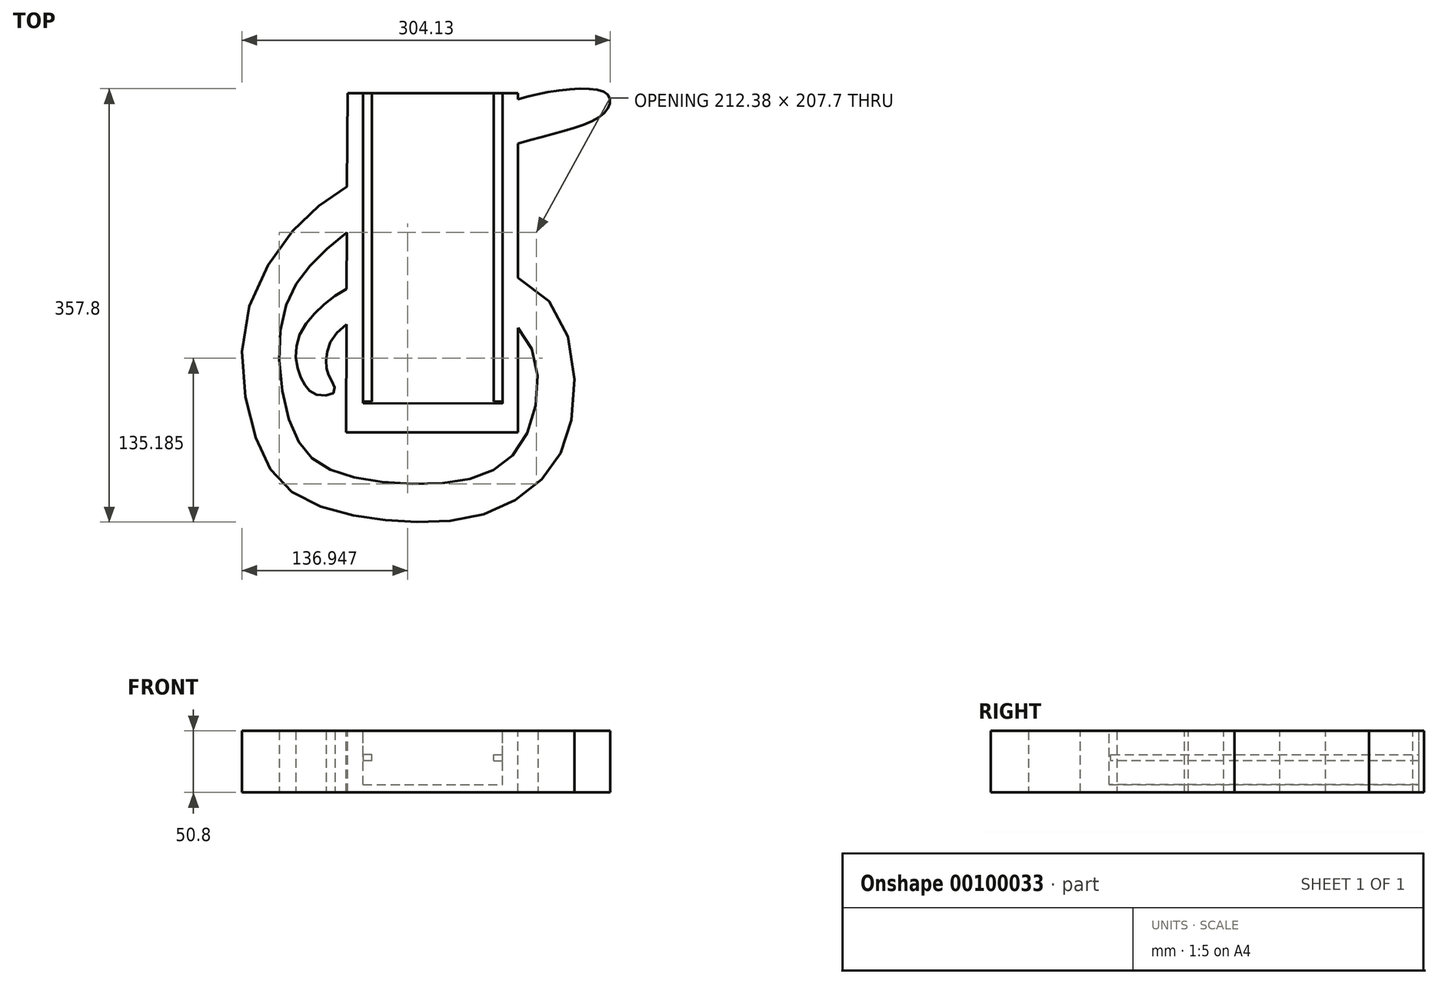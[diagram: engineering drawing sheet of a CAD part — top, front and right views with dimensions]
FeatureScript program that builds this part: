
annotation { "Feature Type Name" : "Feature", "Feature Type Description" : "" }
export const myFeature = defineFeature(function(context is Context, id is Id, definition is map)
    precondition{}
    {
        {
            var Q0;
            Q0=qCreatedBy(makeId("Top.planeOp"),FACE);
            var sketch = newSketch(context, id + "F0", { "sketchPlane" : qUnion([Q0])});
            skFitSpline(sketch, "E0", {"points": [v(166.06, 156.93) * mm, v(168.12, 172.69) * mm, v(103.1, 170.44) * mm, v(46.89, 145.97) * mm, v(-33.8, 103.03) * mm, v(-83.98, 67.54) * mm, v(-129.82, -12.93) * mm, v(-122.29, -110.18) * mm, v(-92.83, -155.39) * mm, v(-41.47, -175.25) * mm, v(9.9, -180.73) * mm, v(66.07, -174.57) * mm, v(115.38, -144.43) * mm, v(139.35, -93.75) * mm, v(127.7, -8.82) * mm, v(61.96, 30.22) * mm, v(-27.08, 19.95) * mm, v(-64.07, 0) * mm, v(-85.75, -26.63) * mm, v(-87.7, -52.22) * mm, v(-81.02, -68.12) * mm, v(-71.97, -75.69) * mm, v(-57.74, -74.4) * mm, v(-57.5, -67.23) * mm, v(-62.34, -58.14) * mm, v(-63.72, -47.19) * mm, v(-58.59, -29.36) * mm, v(-32.56, -8.82) * mm, v(0, 0) * mm, v(56.59, 0) * mm, v(106.48, -38.95) * mm, v(94.83, -120.46) * mm, v(33.88, -148.54) * mm, v(-55.16, -139.64) * mm, v(-90.78, -106.07) * mm, v(-100.37, -15.67) * mm, v(-72.26, 35.68) * mm, v(-10.64, 82.96) * mm, v(87.3, 129.54) * mm, v(166.06, 156.93) * mm]});
            skSolve(sketch);
        }
        {
            var Q0;
            Q0=qSketchRegion(id+"F0",true);
            extrude(context, id + "F1", {"entities" : qUnion([Q0]), "depth" : 50.8 * mm});
        }
        {
            var Q0;
            Q0=makeQuery(id+"F1.opExtrude","CAP_FACE",FACE,{"disambiguationData":[OSD([sQuery(id+"F0.wireOp",EDGE,"E0")])],"isStart":false});
            var sketch = newSketch(context, id + "F2", { "sketchPlane" : qUnion([Q0])});
            skLineSegment(sketch, "E1.top", {"start": v(94.63, 636.97) * mm, "end": v(-46.07, 636.97) * mm});
            skPoint(sketch, "E2", {"position": v(-47.34, -106.85) * mm});
            skLineSegment(sketch, "E3", {"start": v(94.63, -106.85) * mm, "end": v(-47.34, -106.85) * mm});
            skPoint(sketch, "E4", {"position": v(94.63, 173.15) * mm});
            skPoint(sketch, "E5", {"position": v(-46.07, 173.15) * mm});
            skLineSegment(sketch, "E6", {"start": v(-46.07, 173.15) * mm, "end": v(94.63, 173.15) * mm});
            skLineSegment(sketch, "E7", {"start": v(94.63, 173.15) * mm, "end": v(94.63, -106.85) * mm});
            skLineSegment(sketch, "E8", {"start": v(-46.07, 173.15) * mm, "end": v(-47.34, -106.85) * mm});
            skSolve(sketch);
        }
        {
            var Q0;
            {var subQ0=sQuery(id+"F2.wireOp",EDGE,"E6");Q0=makeQuery(id+"F2.imprint","IMPRINT",FACE,{"disambiguationData":[TD([[makeQuery(id+"F2.imprint","IMPRINT",EDGE,{"derivedFrom":subQ0}),-1.0]])]});}
            var Q1;
            {var subQ0=sQuery(id+"F2.wireOp",EDGE,"E1.left");var subQ1=makeQuery(id+"F1.opExtrude","CAP_EDGE",EDGE,{"disambiguationData":[OSD([sQuery(id+"F0.wireOp",EDGE,"E0")])],"isStart":false});var subQ2=makeQuery(id+"F2.imprint","INTERSECT",VERTEX,{"disambiguationData":[OD(1.0)],"derivedFrom":[subQ1,subQ0]});Q1=makeQuery(id+"F2.imprint","IMPRINT",FACE,{"disambiguationData":[TD([[makeQuery(id+"F2.imprint","IMPRINT",EDGE,{"disambiguationData":[TD([[subQ2,-1.0]])],"derivedFrom":subQ0}),1.0]])]});}
            var Q2;
            {var subQ6=sQuery(id+"F2.wireOp",EDGE,"E1.bottom");Q2=makeQuery(id+"F2.imprint","IMPRINT",FACE,{"disambiguationData":[TD([[makeQuery(id+"F2.imprint","IMPRINT",EDGE,{"derivedFrom":subQ6}),-1.0]])]});}
            var Q3;
            {var subQ1=sQuery(id+"F2.wireOp",EDGE,"E1.bottom");Q3=makeQuery(id+"F2.imprint","IMPRINT",FACE,{"disambiguationData":[TD([[makeQuery(id+"F2.imprint","IMPRINT",EDGE,{"derivedFrom":subQ1}),1.0]])]});}
            var Q4;
            {var subQ0=sQuery(id+"F2.wireOp",EDGE,"E3");Q4=makeQuery(id+"F2.imprint","IMPRINT",FACE,{"disambiguationData":[TD([[makeQuery(id+"F2.imprint","IMPRINT",EDGE,{"derivedFrom":subQ0}),-1.0]])]});}
            var Q5;
            {var subQ0=sQuery(id+"F2.wireOp",EDGE,"pUi5V6yo-zhLt-0BLL-0ix0-JjyO4qd6jAw0");var subQ1=makeQuery(id+"F1.opExtrude","CAP_EDGE",EDGE,{"disambiguationData":[OSD([sQuery(id+"F0.wireOp",EDGE,"E0")])],"isStart":false});var subQ2=makeQuery(id+"F2.imprint","INTERSECT",VERTEX,{"disambiguationData":[OD(1.0)],"derivedFrom":[subQ1,subQ0]});Q5=makeQuery(id+"F2.imprint","IMPRINT",FACE,{"disambiguationData":[TD([[makeQuery(id+"F2.imprint","IMPRINT",EDGE,{"disambiguationData":[TD([[subQ2,-1.0]])],"derivedFrom":subQ0}),1.0]])]});}
            var Q6;
            {var subQ1=makeQuery(id+"F1.opExtrude","CAP_EDGE",EDGE,{"disambiguationData":[OSD([sQuery(id+"F0.wireOp",EDGE,"E0")])],"isStart":false});var subQ4=sQuery(id+"F2.wireOp",EDGE,"pUi5V6yo-zhLt-0BLL-0ix0-JjyO4qd6jAw0");var subQ8=makeQuery(id+"F2.imprint","INTERSECT",VERTEX,{"disambiguationData":[OD(0.0)],"derivedFrom":[subQ1,subQ4]});Q6=makeQuery(id+"F2.imprint","IMPRINT",FACE,{"disambiguationData":[TD([[makeQuery(id+"F2.imprint","IMPRINT",EDGE,{"disambiguationData":[TD([[subQ8,-1.0]])],"derivedFrom":subQ4}),1.0]])]});}
            var Q7;
            {var subQ0=sQuery(id+"F2.wireOp",EDGE,"E1.left");var subQ1=makeQuery(id+"F1.opExtrude","CAP_EDGE",EDGE,{"disambiguationData":[OSD([sQuery(id+"F0.wireOp",EDGE,"E0")])],"isStart":false});var subQ2=makeQuery(id+"F2.imprint","INTERSECT",VERTEX,{"disambiguationData":[OD(0.0)],"derivedFrom":[subQ1,subQ0]});Q7=makeQuery(id+"F2.imprint","IMPRINT",FACE,{"disambiguationData":[TD([[makeQuery(id+"F2.imprint","IMPRINT",EDGE,{"disambiguationData":[TD([[subQ2,-1.0]])],"derivedFrom":subQ0}),1.0]])]});}
            var Q8;
            {var subQ0=sQuery(id+"F2.wireOp",EDGE,"E7");var subQ1=makeQuery(id+"F1.opExtrude","CAP_EDGE",EDGE,{"disambiguationData":[OSD([sQuery(id+"F0.wireOp",EDGE,"E0")])],"isStart":false});var subQ2=makeQuery(id+"F2.imprint","INTERSECT",VERTEX,{"disambiguationData":[OD(1.0)],"derivedFrom":[subQ1,subQ0]});Q8=makeQuery(id+"F2.imprint","IMPRINT",FACE,{"disambiguationData":[TD([[makeQuery(id+"F2.imprint","IMPRINT",EDGE,{"disambiguationData":[TD([[subQ2,-1.0]])],"derivedFrom":subQ0}),-1.0]])]});}
            extrude(context, id + "F3", {"entities" : qUnion([Q0, Q1, Q2, Q3, Q4, Q5, Q6, Q7, Q8]), "operationType" : NewBodyOperationType.ADD, "oppositeDirection" : true, "depth" : 50.8 * mm});
        }
        {
            var Q0;
            {var subQ0=sQuery(id+"F2.wireOp",EDGE,"E1.left");var subQ1=sQuery(id+"F0.wireOp",EDGE,"E0");Q0=makeQuery(id+"F3.boolean.opBoolean","MERGE",FACE,{"derivedFrom":[makeQuery(id+"F1.opExtrude","CAP_FACE",FACE,{"disambiguationData":[OSD([subQ1])],"isStart":false}),makeQuery(id+"F3.opExtrude","CAP_FACE",FACE,{"disambiguationData":[OSD([subQ1,subQ0,sQuery(id+"F2.wireOp",EDGE,"pUi5V6yo-zhLt-0BLL-0ix0-JjyO4qd6jAw0"),sQuery(id+"F2.wireOp",EDGE,"CnXaO7K9-1izv-dOOB-x8eX-SiNJ0DRP5LU1"),sQuery(id+"F2.wireOp",EDGE,"E3")])],"isStart":true}),makeQuery(id+"F3.opExtrude","CAP_FACE",FACE,{"disambiguationData":[OSD([subQ1,subQ0,sQuery(id+"F2.wireOp",EDGE,"E1.right"),sQuery(id+"F2.wireOp",EDGE,"E6")])],"isStart":true})]});}
            var sketch = newSketch(context, id + "F4", { "sketchPlane" : qUnion([Q0])});
            skLineSegment(sketch, "E9", {"start": v(81.93, 173.15) * mm, "end": v(-33.37, 173.15) * mm});
            skLineSegment(sketch, "E10", {"start": v(-33.37, 173.15) * mm, "end": v(-33.37, -82.85) * mm});
            skLineSegment(sketch, "E11", {"start": v(-33.37, -82.85) * mm, "end": v(81.93, -82.85) * mm});
            skLineSegment(sketch, "E12", {"start": v(81.93, -82.85) * mm, "end": v(81.93, 173.15) * mm});
            skSolve(sketch);
        }
        {
            var Q0;
            Q0=makeQuery(id+"F4.imprint","IMPRINT",FACE,{"disambiguationData":[TD([[makeQuery(id+"F4.imprint","IMPRINT",EDGE,{"derivedFrom":sQuery(id+"F4.wireOp",EDGE,"E9")}),-1.0]])]});
            extrude(context, id + "F5", {"entities" : qUnion([Q0]), "operationType" : NewBodyOperationType.REMOVE, "oppositeDirection" : true, "depth" : 44.45 * mm});
        }
        {
            var Q0;
            Q0=makeQuery(id+"F5.boolean.opBoolean","COPY",FACE,{"derivedFrom":makeQuery(id+"F5.opExtrude","SWEPT_FACE",FACE,{"disambiguationData":[OSD([sQuery(id+"F4.wireOp",EDGE,"E10")])]})});
            var sketch = newSketch(context, id + "F6", { "sketchPlane" : qUnion([Q0])});
            skLineSegment(sketch, "E13", {"start": v(173.15, 50.8) * mm, "end": v(173.15, 31.08) * mm, "construction": true});
            skLineSegment(sketch, "E14", {"start": v(173.15, 31.08) * mm, "end": v(173.15, 26.07) * mm});
            skLineSegment(sketch, "E15", {"start": v(173.15, 31.08) * mm, "end": v(-81.53, 31.08) * mm});
            skLineSegment(sketch, "E16", {"start": v(-81.53, 31.07) * mm, "end": v(-81.53, 26.07) * mm});
            skLineSegment(sketch, "E17", {"start": v(-81.53, 26.07) * mm, "end": v(173.15, 26.07) * mm});
            skSolve(sketch);
        }
        {
            var Q0;
            Q0=makeQuery(id+"F5.boolean.opBoolean","COPY",FACE,{"derivedFrom":makeQuery(id+"F5.opExtrude","SWEPT_FACE",FACE,{"disambiguationData":[OSD([sQuery(id+"F4.wireOp",EDGE,"E12")])]})});
            var sketch = newSketch(context, id + "F7", { "sketchPlane" : qUnion([Q0])});
            skLineSegment(sketch, "E18", {"start": v(-173.15, 50.8) * mm, "end": v(-173.15, 31.08) * mm, "construction": true});
            skLineSegment(sketch, "E19", {"start": v(-173.15, 26.08) * mm, "end": v(-173.15, 6.35) * mm, "construction": true});
            skLineSegment(sketch, "E20", {"start": v(-173.15, 26.08) * mm, "end": v(-173.15, 31.08) * mm});
            skLineSegment(sketch, "E21", {"start": v(-173.15, 26.07) * mm, "end": v(81.54, 26.07) * mm});
            skLineSegment(sketch, "E22", {"start": v(81.54, 26.08) * mm, "end": v(81.54, 31.08) * mm});
            skLineSegment(sketch, "E23", {"start": v(81.54, 31.08) * mm, "end": v(-173.15, 31.07) * mm});
            skSolve(sketch);
        }
        {
            var Q0;
            Q0=makeQuery(id+"F6.imprint","IMPRINT",FACE,{"disambiguationData":[TD([[makeQuery(id+"F6.imprint","IMPRINT",EDGE,{"derivedFrom":sQuery(id+"F6.wireOp",EDGE,"cu86BMoW-Znzf-g9nx-fHRZ-VvTlNmFD3Y11")}),1.0]])]});
            var Q1;
            Q1=makeQuery(id+"F6.imprint","IMPRINT",FACE,{"disambiguationData":[TD([[makeQuery(id+"F6.imprint","IMPRINT",EDGE,{"derivedFrom":sQuery(id+"F6.wireOp",EDGE,"E14")}),1.0]])]});
            extrude(context, id + "F8", {"entities" : qUnion([Q0, Q1]), "operationType" : NewBodyOperationType.ADD, "depth" : 7.35 * mm});
        }
        {
            var Q0;
            Q0=makeQuery(id+"F7.imprint","IMPRINT",FACE,{"disambiguationData":[TD([[makeQuery(id+"F7.imprint","IMPRINT",EDGE,{"derivedFrom":sQuery(id+"F7.wireOp",EDGE,"hKzRBjoP-kNSg-81Z1-94er-dh69Wtns58Ht")}),-1.0]])]});
            var Q1;
            Q1=makeQuery(id+"F7.imprint","IMPRINT",FACE,{"disambiguationData":[TD([[makeQuery(id+"F7.imprint","IMPRINT",EDGE,{"derivedFrom":sQuery(id+"F7.wireOp",EDGE,"E20")}),-1.0]])]});
            extrude(context, id + "F9", {"entities" : qUnion([Q0, Q1]), "operationType" : NewBodyOperationType.ADD, "depth" : 7.35 * mm});
        }
    });
